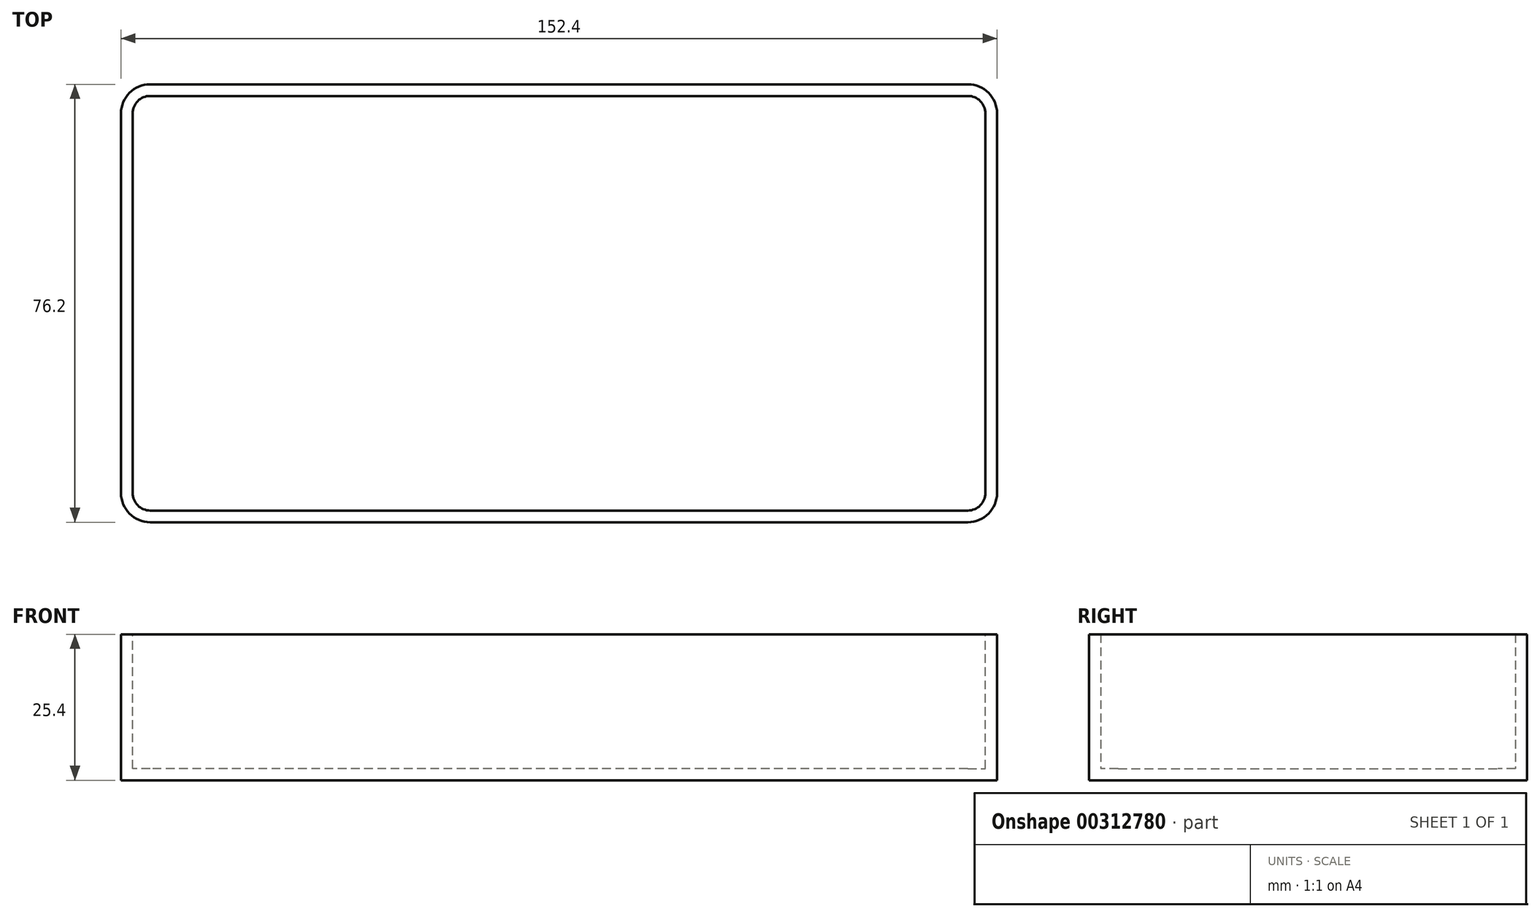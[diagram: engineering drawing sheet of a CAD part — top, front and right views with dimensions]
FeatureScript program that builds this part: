
annotation { "Feature Type Name" : "Feature", "Feature Type Description" : "" }
export const myFeature = defineFeature(function(context is Context, id is Id, definition is map)
    precondition{}
    {
        {
            var Q0;
            Q0=qCreatedBy(makeId("Top.planeOp"),FACE);
            var sketch = newSketch(context, id + "F0", { "sketchPlane" : qUnion([Q0])});
            skLineSegment(sketch, "E0.bottom", {"start": v(-6.35, 0) * mm, "end": v(-158.75, 0) * mm});
            skLineSegment(sketch, "E0.top", {"start": v(-6.35, 76.2) * mm, "end": v(-158.75, 76.2) * mm});
            skLineSegment(sketch, "E0.left", {"start": v(-6.35, 0) * mm, "end": v(-6.35, 76.2) * mm});
            skLineSegment(sketch, "E0.right", {"start": v(-158.75, 0) * mm, "end": v(-158.75, 76.2) * mm});
            skSolve(sketch);
        }
        {
            var Q0;
            Q0=makeQuery(id+"F0.imprint","IMPRINT",FACE,{"disambiguationData":[TD([[makeQuery(id+"F0.imprint","IMPRINT",EDGE,{"derivedFrom":sQuery(id+"F0.wireOp",EDGE,"E0.bottom")}),-1.0]])]});
            extrude(context, id + "F1", {"entities" : qUnion([Q0]), "depth" : 25.4 * mm});
        }
        {
            var Q0;
            Q0=makeQuery(id+"F1.opExtrude","SWEPT_EDGE",EDGE,{"disambiguationData":[OSD([sQuery(id+"F0.wireOp",EDGE,"E0.bottom"),sQuery(id+"F0.wireOp",EDGE,"E0.right")])]});
            var Q1;
            Q1=makeQuery(id+"F1.opExtrude","SWEPT_EDGE",EDGE,{"disambiguationData":[OSD([sQuery(id+"F0.wireOp",EDGE,"E0.bottom"),sQuery(id+"F0.wireOp",EDGE,"E0.left")])]});
            var Q2;
            Q2=makeQuery(id+"F1.opExtrude","SWEPT_EDGE",EDGE,{"disambiguationData":[OSD([sQuery(id+"F0.wireOp",EDGE,"E0.top"),sQuery(id+"F0.wireOp",EDGE,"E0.right")])]});
            var Q3;
            Q3=makeQuery(id+"F1.opExtrude","SWEPT_EDGE",EDGE,{"disambiguationData":[OSD([sQuery(id+"F0.wireOp",EDGE,"E0.top"),sQuery(id+"F0.wireOp",EDGE,"E0.left")])]});
            fillet(context, id + "F2", {"entities" : qUnion([Q0, Q1, Q2, Q3]), "radius" : 5.08 * mm, "tangentPropagation" : true, "allowEdgeOverflow" : false});
        }
        {
            var Q0;
            Q0=makeQuery(id+"F1.opExtrude","CAP_FACE",FACE,{"disambiguationData":[OSD([sQuery(id+"F0.wireOp",EDGE,"E0.bottom"),sQuery(id+"F0.wireOp",EDGE,"E0.top"),sQuery(id+"F0.wireOp",EDGE,"E0.left"),sQuery(id+"F0.wireOp",EDGE,"E0.right")])],"isStart":false});
            shell(context, id + "F3", {"entities" : qUnion([Q0]), "thickness" : 2.03 * mm});
        }
    });
